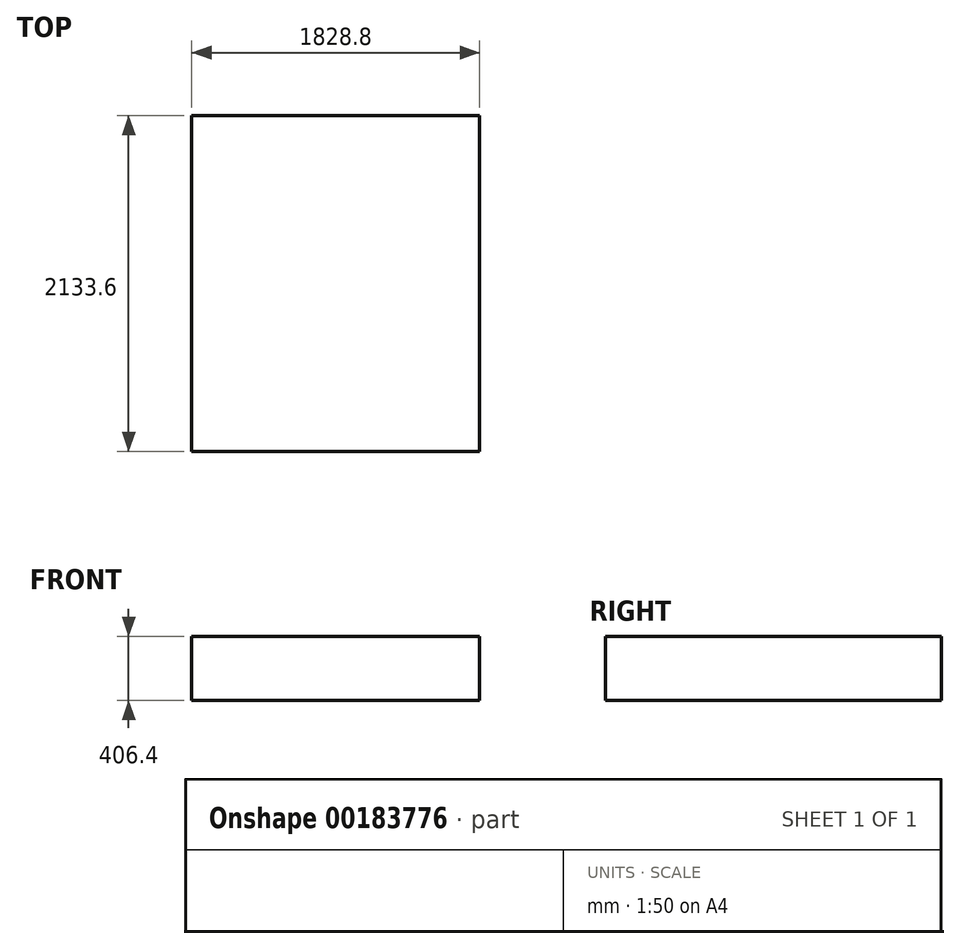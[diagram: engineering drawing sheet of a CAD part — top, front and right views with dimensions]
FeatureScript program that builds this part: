
annotation { "Feature Type Name" : "Feature", "Feature Type Description" : "" }
export const myFeature = defineFeature(function(context is Context, id is Id, definition is map)
    precondition{}
    {
        {
            var Q0;
            Q0=qCreatedBy(makeId("Top.planeOp"),FACE);
            var sketch = newSketch(context, id + "F0", { "sketchPlane" : qUnion([Q0])});
            skLineSegment(sketch, "E0.bottom", {"start": v(-1828.8, 2133.6) * mm, "end": v(0, 2133.6) * mm});
            skLineSegment(sketch, "E0.top", {"start": v(-1828.8, 0) * mm, "end": v(0, 0) * mm});
            skLineSegment(sketch, "E0.left", {"start": v(-1828.8, 2133.6) * mm, "end": v(-1828.8, 0) * mm});
            skLineSegment(sketch, "E0.right", {"start": v(0, 2133.6) * mm, "end": v(0, 0) * mm});
            skSolve(sketch);
        }
        {
            var Q0;
            Q0=makeQuery(id+"F0.imprint","IMPRINT",FACE,{"disambiguationData":[TD([[makeQuery(id+"F0.imprint","IMPRINT",EDGE,{"derivedFrom":sQuery(id+"F0.wireOp",EDGE,"E0.bottom")}),-1.0]])]});
            extrude(context, id + "F1", {"entities" : qUnion([Q0]), "depth" : 406.4 * mm});
        }
    });
